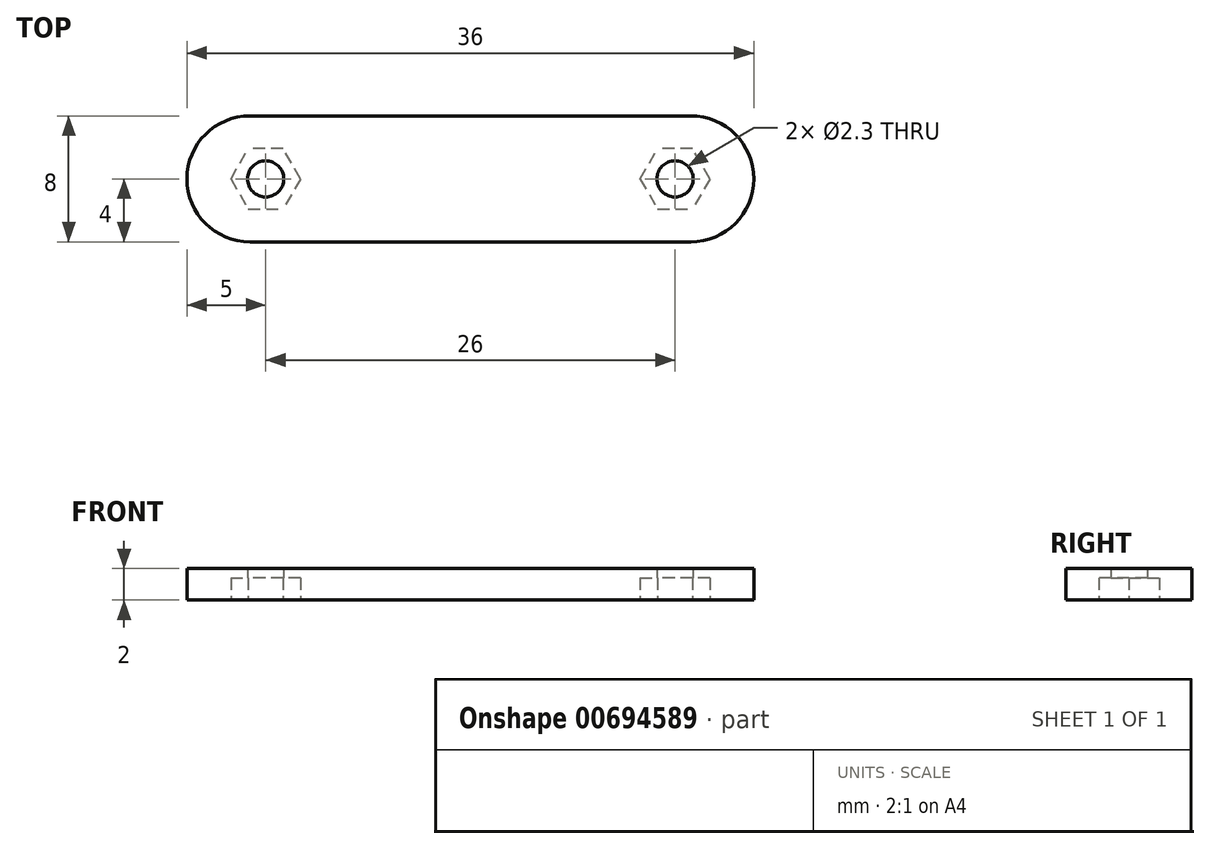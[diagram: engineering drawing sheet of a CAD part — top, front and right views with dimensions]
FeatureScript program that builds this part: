
annotation { "Feature Type Name" : "Feature", "Feature Type Description" : "" }
export const myFeature = defineFeature(function(context is Context, id is Id, definition is map)
    precondition{}
    {
        {
            var Q0;
            Q0=qCreatedBy(makeId("Top.planeOp"),FACE);
            var sketch = newSketch(context, id + "F0", { "sketchPlane" : qUnion([Q0])});
            skCircle(sketch, "E0", {"center": v(-13, 0) * mm, "radius": 1.15 * mm});
            skCircle(sketch, "E1.MirrorC", {"center": v(13, 0) * mm, "radius": 1.15 * mm});
            skSolve(sketch);
        }
        {
            var Q0;
            Q0=qCreatedBy(makeId("Top.planeOp"),FACE);
            var sketch = newSketch(context, id + "F1", { "sketchPlane" : qUnion([Q0])});
            skLineSegment(sketch, "E2.bottom", {"start": v(18, 4) * mm, "end": v(-18, 4) * mm});
            skLineSegment(sketch, "E2.top", {"start": v(18, -4) * mm, "end": v(-18, -4) * mm});
            skLineSegment(sketch, "E2.left", {"start": v(18, 4) * mm, "end": v(18, -4) * mm});
            skLineSegment(sketch, "E2.right", {"start": v(-18, 4) * mm, "end": v(-18, -4) * mm});
            skPoint(sketch, "E2.middle", {"position": v(0, 0) * mm});
            skSolve(sketch);
        }
        {
            var Q0;
            Q0=qCreatedBy(makeId("Top.planeOp"),FACE);
            var sketch = newSketch(context, id + "F2", { "sketchPlane" : qUnion([Q0])});
            skLineSegment(sketch, "E3", {"start": v(-13, 0) * mm, "end": v(-13, 4.8) * mm, "construction": true});
            skLineSegment(sketch, "E4", {"start": v(-13, 0) * mm, "end": v(-5.64, 0) * mm, "construction": true});
            skLineSegment(sketch, "E5", {"start": v(-13, 0) * mm, "end": v(-15.53, 4.38) * mm, "construction": true});
            skLineSegment(sketch, "E6", {"start": v(-10.79, 0) * mm, "end": v(-11.9, 1.91) * mm});
            skLineSegment(sketch, "E7", {"start": v(-11.9, 1.91) * mm, "end": v(-13, 1.91) * mm});
            skLineSegment(sketch, "E8.MirrorCS", {"start": v(-14.1, 1.91) * mm, "end": v(-13, 1.91) * mm});
            skLineSegment(sketch, "E9.MirrorCS", {"start": v(-15.21, 0) * mm, "end": v(-14.1, 1.91) * mm});
            skLineSegment(sketch, "E10.MirrorCS", {"start": v(-10.79, 0) * mm, "end": v(-11.9, -1.91) * mm});
            skLineSegment(sketch, "E11.MirrorCS", {"start": v(-11.9, -1.91) * mm, "end": v(-13, -1.91) * mm});
            skLineSegment(sketch, "E12.MirrorCS", {"start": v(-14.1, -1.91) * mm, "end": v(-13, -1.91) * mm});
            skLineSegment(sketch, "E13.MirrorCS", {"start": v(-15.21, 0) * mm, "end": v(-14.1, -1.91) * mm});
            skLineSegment(sketch, "E14.MirrorCS", {"start": v(15.21, 0) * mm, "end": v(14.1, -1.91) * mm});
            skLineSegment(sketch, "E15.MirrorCS", {"start": v(14.1, -1.91) * mm, "end": v(13, -1.91) * mm});
            skLineSegment(sketch, "E16.MirrorCS", {"start": v(14.1, 1.91) * mm, "end": v(13, 1.91) * mm});
            skLineSegment(sketch, "E17.MirrorCS", {"start": v(10.79, 0) * mm, "end": v(11.9, 1.91) * mm});
            skLineSegment(sketch, "E18.MirrorCS", {"start": v(15.21, 0) * mm, "end": v(14.1, 1.91) * mm});
            skLineSegment(sketch, "E19.MirrorCS", {"start": v(11.9, 1.91) * mm, "end": v(13, 1.91) * mm});
            skLineSegment(sketch, "E20.MirrorCS", {"start": v(11.9, -1.91) * mm, "end": v(13, -1.91) * mm});
            skLineSegment(sketch, "E21.MirrorCS", {"start": v(10.79, 0) * mm, "end": v(11.9, -1.91) * mm});
            skSolve(sketch);
        }
        {
            var Q0;
            Q0 = qSketchRegion(id + "F1", true);
            extrude(context, id + "F3", {"entities" : qUnion([Q0]), "depth" : 2 * mm, "offsetDistance" : 25 * mm});
        }
        {
            var Q0;
            Q0 = qSketchRegion(id + "F0", true);
            extrude(context, id + "F4", {"entities" : qUnion([Q0]), "operationType" : NewBodyOperationType.REMOVE, "endBound" : BoundingType.THROUGH_ALL, "depth" : 25 * mm, "offsetDistance" : 25 * mm});
        }
        {
            var Q0;
            Q0 = qSketchRegion(id + "F2", true);
            extrude(context, id + "F5", {"entities" : qUnion([Q0]), "operationType" : NewBodyOperationType.REMOVE, "depth" : 1.4 * mm, "offsetDistance" : 25 * mm});
        }
        {
            var Q0;
            Q0=makeQuery(id+"F3.opExtrude","SWEPT_EDGE",EDGE,{"disambiguationData":[OSD([sQuery(id+"F1.wireOp",EDGE,"E2.bottom"),sQuery(id+"F1.wireOp",EDGE,"E2.right")])]});
            var Q1;
            Q1=makeQuery(id+"F3.opExtrude","SWEPT_EDGE",EDGE,{"disambiguationData":[OSD([sQuery(id+"F1.wireOp",EDGE,"E2.top"),sQuery(id+"F1.wireOp",EDGE,"E2.right")])]});
            var Q2;
            Q2=makeQuery(id+"F3.opExtrude","SWEPT_EDGE",EDGE,{"disambiguationData":[OSD([sQuery(id+"F1.wireOp",EDGE,"E2.top"),sQuery(id+"F1.wireOp",EDGE,"E2.left")])]});
            var Q3;
            Q3=makeQuery(id+"F3.opExtrude","SWEPT_EDGE",EDGE,{"disambiguationData":[OSD([sQuery(id+"F1.wireOp",EDGE,"E2.bottom"),sQuery(id+"F1.wireOp",EDGE,"E2.left")])]});
            fillet(context, id + "F6", {"entities" : qUnion([Q0, Q1, Q2, Q3]), "radius" : 4 * mm, "tangentPropagation" : true, "allowEdgeOverflow" : false});
        }
    });
